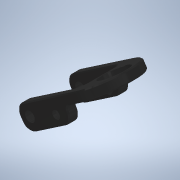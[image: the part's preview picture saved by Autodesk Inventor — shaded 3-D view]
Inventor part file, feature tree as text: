
AUTODESK INVENTOR PART (.ipt)
format: ipt  version: 2020 (Build 240168000, 168)  size: 225,792 bytes
history: native  units: mm
features: extrude x1, sketch x1
ambient origin geometry x8: Origin, YZ Plane, XZ Plane, XY Plane, X Axis, Y Axis, Z Axis, Center Point
bodies: Volumenkörper1 (feature_tree), Body1 (feature_tree)
feature tree (2):
  extrude  "Extrusion2"  Depth=10.0mm TaperAngle=0.0deg
  sketch  "Skizze2"  dims[d3=12.0mm d4=10.0mm d5=0.0mm]
